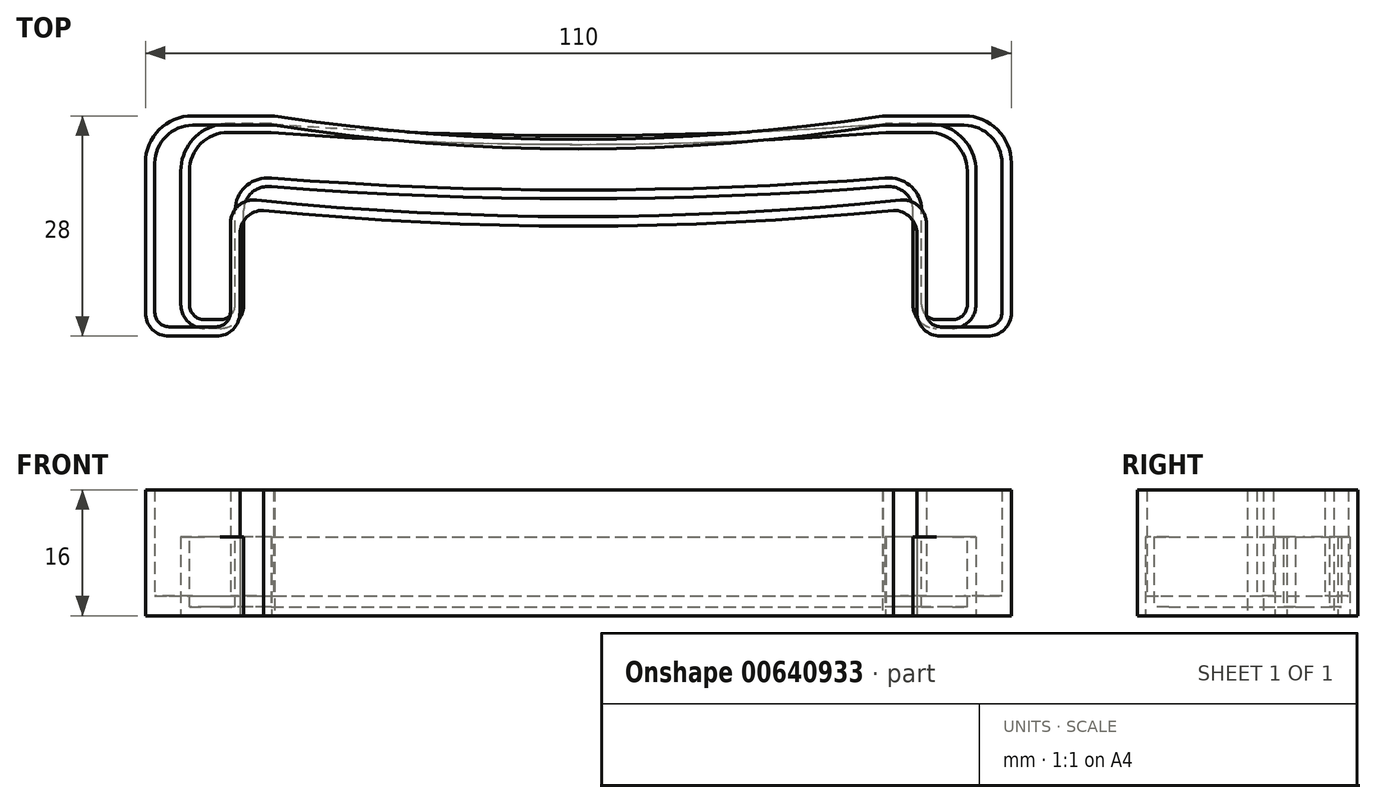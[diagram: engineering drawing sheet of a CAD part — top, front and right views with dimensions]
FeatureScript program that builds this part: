
annotation { "Feature Type Name" : "Feature", "Feature Type Description" : "" }
export const myFeature = defineFeature(function(context is Context, id is Id, definition is map)
    precondition{}
    {
        {
            var Q0;
            Q0=qCreatedBy(makeId("Top.planeOp"),FACE);
            var sketch = newSketch(context, id + "F0", { "sketchPlane" : qUnion([Q0])});
            skLineSegment(sketch, "E0.bottom", {"start": v(49, 14) * mm, "end": v(38.61, 14) * mm});
            skLineSegment(sketch, "E0.top", {"start": v(52, -14) * mm, "end": v(46, -14) * mm});
            skLineSegment(sketch, "E0.left", {"start": v(55, 8) * mm, "end": v(55, -11) * mm});
            skLineSegment(sketch, "E0.right", {"start": v(-55, 8) * mm, "end": v(-55, -11) * mm});
            skPoint(sketch, "E0.middle", {"position": v(0, 0) * mm});
            skPoint(sketch, "E1.visualSharp", {"position": v(-55, 14) * mm});
            skArc(sketch, "E1.filletArc", {"start": v(-49, 14) * mm, "mid": v(-53.24, 12.24) * mm, "end": v(-55, 8) * mm});
            skPoint(sketch, "E2.visualSharp", {"position": v(55, 14) * mm});
            skArc(sketch, "E2.filletArc", {"start": v(55, 8) * mm, "mid": v(53.24, 12.24) * mm, "end": v(49, 14) * mm});
            skArc(sketch, "E3", {"start": v(-38.61, 14) * mm, "mid": v(0, 11) * mm, "end": v(38.61, 14) * mm});
            skLineSegment(sketch, "E4.trimOffspring", {"start": v(-38.61, 14) * mm, "end": v(-49, 14) * mm});
            skLineSegment(sketch, "E5.left", {"start": v(43, -1) * mm, "end": v(43, -11) * mm});
            skLineSegment(sketch, "E5.right", {"start": v(-43, -1) * mm, "end": v(-43, -11) * mm});
            skPoint(sketch, "E5.middle", {"position": v(0, -14) * mm});
            skLineSegment(sketch, "E6.trimOffspring", {"start": v(-46, -14) * mm, "end": v(-52, -14) * mm});
            skPoint(sketch, "E7.orphan", {"position": v(-43, -30) * mm});
            skPoint(sketch, "E8.orphan", {"position": v(43, -30) * mm});
            skPoint(sketch, "E9.visualSharp", {"position": v(-43, 2) * mm});
            skArc(sketch, "E9.filletArc", {"start": v(-40, 2) * mm, "mid": v(-42.12, 1.12) * mm, "end": v(-43, -1) * mm});
            skPoint(sketch, "E10.visualSharp", {"position": v(43, 2) * mm});
            skArc(sketch, "E10.filletArc", {"start": v(43, -1) * mm, "mid": v(42.12, 1.12) * mm, "end": v(40, 2) * mm});
            skPoint(sketch, "E11.visualSharp", {"position": v(43, -14) * mm});
            skArc(sketch, "E11.filletArc", {"start": v(43, -11) * mm, "mid": v(43.88, -13.12) * mm, "end": v(46, -14) * mm});
            skPoint(sketch, "E12.visualSharp", {"position": v(-43, -14) * mm});
            skArc(sketch, "E12.filletArc", {"start": v(-46, -14) * mm, "mid": v(-43.88, -13.12) * mm, "end": v(-43, -11) * mm});
            skPoint(sketch, "E13.visualSharp", {"position": v(-55, -14) * mm});
            skArc(sketch, "E13.filletArc", {"start": v(-55, -11) * mm, "mid": v(-54.12, -13.12) * mm, "end": v(-52, -14) * mm});
            skPoint(sketch, "E14.visualSharp", {"position": v(55, -14) * mm});
            skArc(sketch, "E14.filletArc", {"start": v(52, -14) * mm, "mid": v(54.12, -13.12) * mm, "end": v(55, -11) * mm});
            skArc(sketch, "E15", {"start": v(-40, 2) * mm, "mid": v(0, 0) * mm, "end": v(40, 2) * mm});
            skLineSegment(sketch, "E16.0", {"start": v(52, -12.8) * mm, "end": v(46, -12.8) * mm});
            skArc(sketch, "E16.1", {"start": v(44.2, -11) * mm, "mid": v(44.73, -12.27) * mm, "end": v(46, -12.8) * mm});
            skLineSegment(sketch, "E16.2", {"start": v(44.2, 0.31) * mm, "end": v(44.2, -11) * mm});
            skArc(sketch, "E16.3", {"start": v(-40.9, 3.3) * mm, "mid": v(0, 1.2) * mm, "end": v(40.9, 3.3) * mm});
            skLineSegment(sketch, "E16.4", {"start": v(-44.2, 0.31) * mm, "end": v(-44.2, -11) * mm});
            skArc(sketch, "E16.5", {"start": v(-38.7, 12.8) * mm, "mid": v(0, 9.8) * mm, "end": v(38.7, 12.8) * mm});
            skLineSegment(sketch, "E16.6", {"start": v(49, 12.8) * mm, "end": v(38.7, 12.8) * mm});
            skArc(sketch, "E16.7", {"start": v(53.8, 8) * mm, "mid": v(52.4, 11.4) * mm, "end": v(49, 12.8) * mm});
            skLineSegment(sketch, "E16.8", {"start": v(53.8, 8) * mm, "end": v(53.8, -11) * mm});
            skLineSegment(sketch, "E16.9", {"start": v(-38.7, 12.8) * mm, "end": v(-49, 12.8) * mm});
            skArc(sketch, "E16.10", {"start": v(-49, 12.8) * mm, "mid": v(-52.4, 11.4) * mm, "end": v(-53.8, 8) * mm});
            skLineSegment(sketch, "E16.11", {"start": v(-53.8, 8) * mm, "end": v(-53.8, -11) * mm});
            skArc(sketch, "E16.12", {"start": v(-53.8, -11) * mm, "mid": v(-53.27, -12.27) * mm, "end": v(-52, -12.8) * mm});
            skLineSegment(sketch, "E16.13", {"start": v(-46, -12.8) * mm, "end": v(-52, -12.8) * mm});
            skArc(sketch, "E16.14", {"start": v(52, -12.8) * mm, "mid": v(53.27, -12.27) * mm, "end": v(53.8, -11) * mm});
            skArc(sketch, "E16.15", {"start": v(-46, -12.8) * mm, "mid": v(-44.73, -12.27) * mm, "end": v(-44.2, -11) * mm});
            skPoint(sketch, "E17.visualSharp", {"position": v(-44.2, 3.65) * mm});
            skArc(sketch, "E17.filletArc", {"start": v(-40.9, 3.3) * mm, "mid": v(-43.2, 2.54) * mm, "end": v(-44.2, 0.31) * mm});
            skPoint(sketch, "E18.visualSharp", {"position": v(44.2, 3.65) * mm});
            skArc(sketch, "E18.filletArc", {"start": v(44.2, 0.31) * mm, "mid": v(43.2, 2.54) * mm, "end": v(40.9, 3.3) * mm});
            skSolve(sketch);
        }
        {
            var Q0;
            Q0=makeQuery(id+"F0.imprint","IMPRINT",FACE,{"disambiguationData":[TD([[makeQuery(id+"F0.imprint","IMPRINT",EDGE,{"derivedFrom":sQuery(id+"F0.wireOp",EDGE,"E0.bottom")}),1.0]])]});
            var Q1;
            Q1=makeQuery(id+"F0.imprint","IMPRINT",FACE,{"disambiguationData":[TD([[makeQuery(id+"F0.imprint","IMPRINT",EDGE,{"derivedFrom":sQuery(id+"F0.wireOp",EDGE,"E16.0")}),-1.0]])]});
            extrude(context, id + "F1", {"entities" : qUnion([Q0, Q1]), "depth" : 2.5 * mm, "offsetDistance" : 25 * mm});
        }
        {
            var Q0;
            Q0=makeQuery(id+"F0.imprint","IMPRINT",FACE,{"disambiguationData":[TD([[makeQuery(id+"F0.imprint","IMPRINT",EDGE,{"derivedFrom":sQuery(id+"F0.wireOp",EDGE,"E0.bottom")}),1.0]])]});
            extrude(context, id + "F2", {"entities" : qUnion([Q0]), "operationType" : NewBodyOperationType.ADD, "depth" : 16 * mm, "offsetDistance" : 25 * mm});
        }
        {
            var Q0;
            Q0=qCreatedBy(makeId("Top.planeOp"),FACE);
            var sketch = newSketch(context, id + "F3", { "sketchPlane" : qUnion([Q0])});
            skLineSegment(sketch, "E19.bottom", {"start": v(47.5, -13) * mm, "end": v(45.5, -13) * mm});
            skLineSegment(sketch, "E19.top", {"start": v(44.5, 13) * mm, "end": v(-44.5, 13) * mm});
            skLineSegment(sketch, "E19.left", {"start": v(50.5, -10) * mm, "end": v(50.5, 7) * mm});
            skLineSegment(sketch, "E19.right", {"start": v(-50.5, -10) * mm, "end": v(-50.5, 7) * mm});
            skPoint(sketch, "E19.middle", {"position": v(0, 0) * mm});
            skLineSegment(sketch, "E20.bottom", {"start": v(42.5, -31) * mm, "end": v(-42.5, -31) * mm});
            skLineSegment(sketch, "E20.top", {"start": v(39.5, 5) * mm, "end": v(-39.5, 5) * mm});
            skLineSegment(sketch, "E20.left", {"start": v(42.5, -10) * mm, "end": v(42.5, 2) * mm});
            skLineSegment(sketch, "E20.right", {"start": v(-42.5, -10) * mm, "end": v(-42.5, 2) * mm});
            skPoint(sketch, "E20.middle", {"position": v(0, -13) * mm});
            skLineSegment(sketch, "E21.bottom", {"start": v(39, 23.71) * mm, "end": v(-39, 23.71) * mm});
            skLineSegment(sketch, "E21.top", {"start": v(39, -23.71) * mm, "end": v(-39, -23.71) * mm});
            skLineSegment(sketch, "E21.left", {"start": v(39, 23.71) * mm, "end": v(39, -23.71) * mm});
            skLineSegment(sketch, "E21.right", {"start": v(-39, 23.71) * mm, "end": v(-39, -23.71) * mm});
            skArc(sketch, "E22", {"start": v(-39, 13) * mm, "mid": v(0, 11.48) * mm, "end": v(39, 13) * mm});
            skArc(sketch, "E23", {"start": v(-39, 5) * mm, "mid": v(0, 3.48) * mm, "end": v(39, 5) * mm});
            skPoint(sketch, "E24.visualSharp", {"position": v(-50.5, 13) * mm});
            skArc(sketch, "E24.filletArc", {"start": v(-44.5, 13) * mm, "mid": v(-48.74, 11.24) * mm, "end": v(-50.5, 7) * mm});
            skPoint(sketch, "E25.visualSharp", {"position": v(50.5, 13) * mm});
            skArc(sketch, "E25.filletArc", {"start": v(50.5, 7) * mm, "mid": v(48.74, 11.24) * mm, "end": v(44.5, 13) * mm});
            skPoint(sketch, "E26.visualSharp", {"position": v(-42.5, 5) * mm});
            skArc(sketch, "E26.filletArc", {"start": v(-39.5, 5) * mm, "mid": v(-41.62, 4.12) * mm, "end": v(-42.5, 2) * mm});
            skPoint(sketch, "E27.visualSharp", {"position": v(-50.5, -13) * mm});
            skArc(sketch, "E27.filletArc", {"start": v(-50.5, -10) * mm, "mid": v(-49.62, -12.12) * mm, "end": v(-47.5, -13) * mm});
            skPoint(sketch, "E28.visualSharp", {"position": v(42.5, 5) * mm});
            skArc(sketch, "E28.filletArc", {"start": v(42.5, 2) * mm, "mid": v(41.62, 4.12) * mm, "end": v(39.5, 5) * mm});
            skPoint(sketch, "E29", {"position": v(-42.5, -13) * mm});
            skPoint(sketch, "E30", {"position": v(42.5, -13) * mm});
            skLineSegment(sketch, "E31.trimOffspring", {"start": v(-45.5, -13) * mm, "end": v(-47.5, -13) * mm});
            skLineSegment(sketch, "E32.trimOffspring", {"start": v(39, -13) * mm, "end": v(-39, -13) * mm});
            skPoint(sketch, "E33.visualSharp", {"position": v(50.5, -13) * mm});
            skArc(sketch, "E33.filletArc", {"start": v(47.5, -13) * mm, "mid": v(49.62, -12.12) * mm, "end": v(50.5, -10) * mm});
            skArc(sketch, "E34.filletArc", {"start": v(42.5, -10) * mm, "mid": v(43.38, -12.12) * mm, "end": v(45.5, -13) * mm});
            skArc(sketch, "E35.filletArc", {"start": v(-45.5, -13) * mm, "mid": v(-43.38, -12.12) * mm, "end": v(-42.5, -10) * mm});
            skSolve(sketch);
        }
        {
            var Q0;
            Q0=makeQuery(id+"F3.imprint","IMPRINT",FACE,{"disambiguationData":[TD([[makeQuery(id+"F3.imprint","IMPRINT",EDGE,{"derivedFrom":sQuery(id+"F3.wireOp",EDGE,"E19.right")}),-1.0]])]});
            var Q1;
            {var subQ0=sQuery(id+"F3.wireOp",EDGE,"E20.top");Q1=makeQuery(id+"F3.imprint","IMPRINT",FACE,{"disambiguationData":[TD([[makeQuery(id+"F3.imprint","IMPRINT",EDGE,{"derivedFrom":subQ0}),-1.0]])]});}
            var Q2;
            Q2=makeQuery(id+"F3.imprint","IMPRINT",FACE,{"disambiguationData":[TD([[makeQuery(id+"F3.imprint","IMPRINT",EDGE,{"derivedFrom":sQuery(id+"F3.wireOp",EDGE,"E19.bottom")}),-1.0]])]});
            var Q3;
            Q3=makeQuery(id+"F3.imprint","IMPRINT",FACE,{"disambiguationData":[TD([[makeQuery(id+"F3.imprint","IMPRINT",EDGE,{"derivedFrom":sQuery(id+"F3.wireOp",EDGE,"E20.top")}),1.0]])]});
            extrude(context, id + "F4", {"entities" : qUnion([Q0, Q1, Q2, Q3]), "depth" : 10 * mm, "offsetDistance" : 25 * mm});
        }
        {
            var Q0;
            Q0=makeQuery(id+"F4.opExtrude","CAP_FACE",FACE,{"disambiguationData":[OSD([sQuery(id+"F3.wireOp",EDGE,"E19.bottom"),sQuery(id+"F3.wireOp",EDGE,"E19.top"),sQuery(id+"F3.wireOp",EDGE,"E19.left"),sQuery(id+"F3.wireOp",EDGE,"E19.right"),sQuery(id+"F3.wireOp",EDGE,"E20.left"),sQuery(id+"F3.wireOp",EDGE,"E20.right"),sQuery(id+"F3.wireOp",EDGE,"E22"),sQuery(id+"F3.wireOp",EDGE,"E23"),sQuery(id+"F3.wireOp",EDGE,"E24.filletArc"),sQuery(id+"F3.wireOp",EDGE,"E25.filletArc"),sQuery(id+"F3.wireOp",EDGE,"E26.filletArc"),sQuery(id+"F3.wireOp",EDGE,"E27.filletArc"),sQuery(id+"F3.wireOp",EDGE,"E28.filletArc"),sQuery(id+"F3.wireOp",EDGE,"E31.trimOffspring"),sQuery(id+"F3.wireOp",EDGE,"E33.filletArc"),sQuery(id+"F3.wireOp",EDGE,"E34.filletArc"),sQuery(id+"F3.wireOp",EDGE,"E35.filletArc")])],"isStart":false});
            shell(context, id + "F5", {"entities" : qUnion([Q0]), "thickness" : 1.1 * mm});
        }
    });
